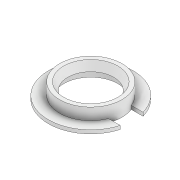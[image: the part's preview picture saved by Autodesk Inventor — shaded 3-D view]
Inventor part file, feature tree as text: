
AUTODESK INVENTOR PART (.ipt)
format: ipt  version: 2022.3 (Build 263350000, 350)  size: 130,560 bytes
history: native  units: mm
features: sketch x5, extrude x3, other x1, sweep x1
ambient origin geometry x8: Origin, YZ Plane, XZ Plane, XY Plane, X Axis, Y Axis, Z Axis, Center Point
bodies: Body1 (feature_tree)
feature tree (10):
  other  "Sólido1"
  extrude  "Extrusión1"  Depth=19.5mm
  extrude  "Extrusión2"  Depth=1.5mm
  extrude  "Extrusión3"  Depth=5.0mm
  sweep  "Barrido1"
  sketch  "Boceto1"  dims[d0=36.0mm d1=19.5mm]
  sketch  "Boceto2"  dims[d5=5.0mm d6=0.0mm d7=4.85mm]
  sketch  "Boceto3"  dims[d8=4.85mm d9=5.0mm d10=0.0mm]
  sketch  "Boceto4"  dims[d11=0.0mm d12=0.0mm]
  sketch  "Boceto 3D1"  dims[d2=1.5mm d3=0.0mm d4=26.5mm]
